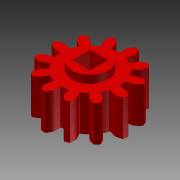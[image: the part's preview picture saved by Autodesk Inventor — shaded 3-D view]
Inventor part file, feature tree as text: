
AUTODESK INVENTOR PART (.ipt)
format: ipt  version: 2013 (Build 170138000, 138)  size: 462,336 bytes
history: native  units: mm (DEFAULTED — no unit token found)
features: imported_body x1, plane x1
ambient origin geometry x8: Origin, YZ Plane, XZ Plane, XY Plane, X Axis, Y Axis, Z Axis, Center Point
bodies: Solid1 (feature_tree)
feature tree (2):
  imported_body  "Base1"
  plane  "Work Plane1"
